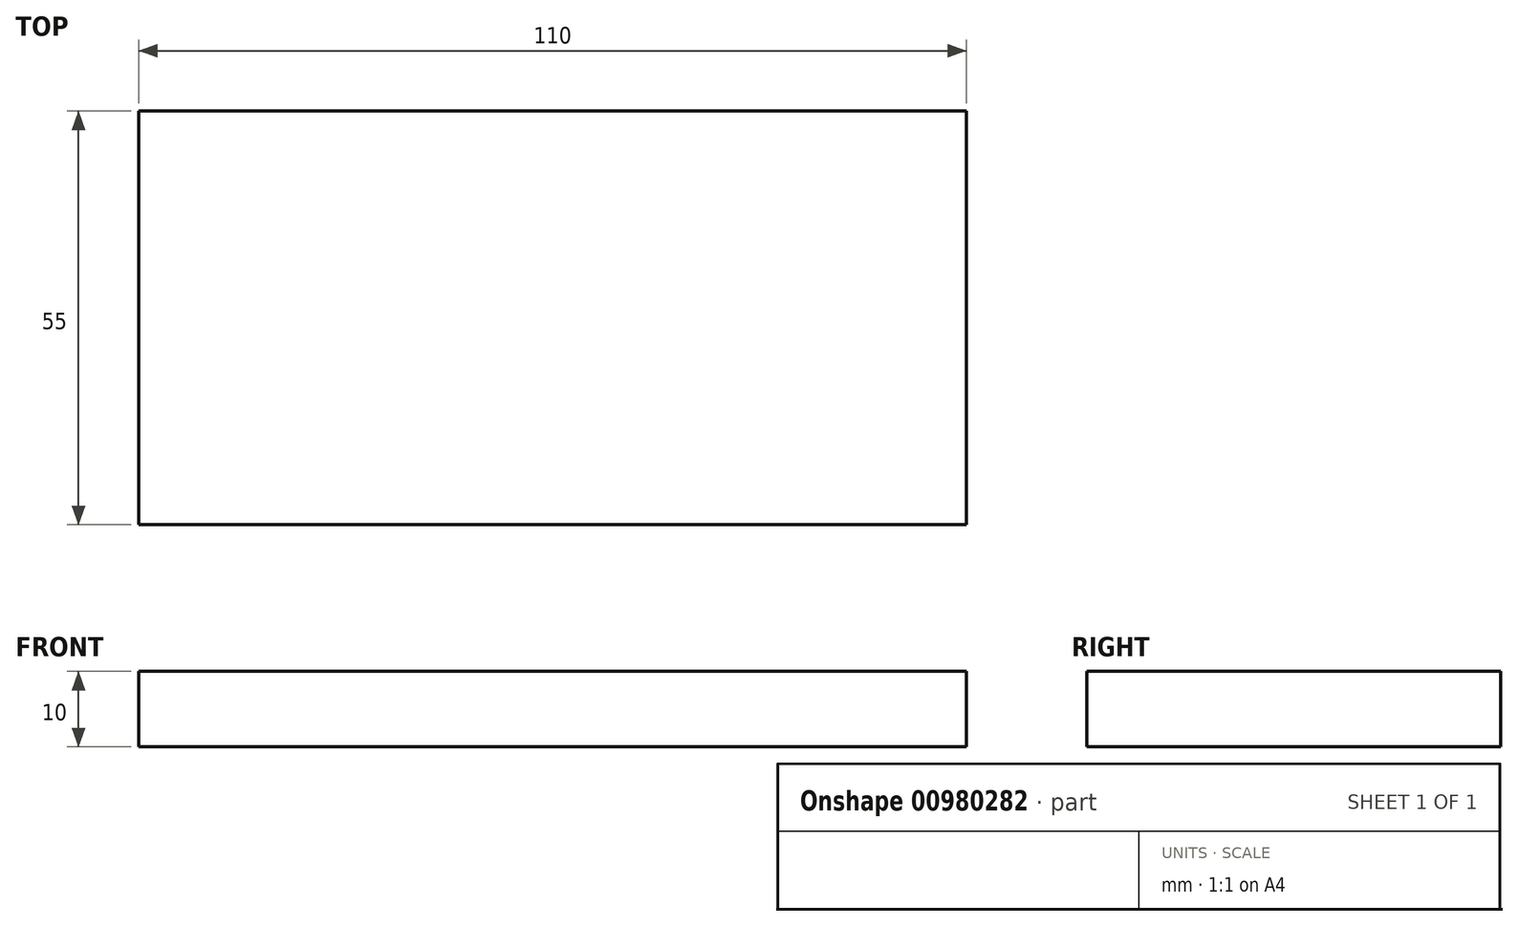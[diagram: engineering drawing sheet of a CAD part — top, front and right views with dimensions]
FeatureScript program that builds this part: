
annotation { "Feature Type Name" : "Feature", "Feature Type Description" : "" }
export const myFeature = defineFeature(function(context is Context, id is Id, definition is map)
    precondition{}
    {
        {
            var Q0;
            Q0=qCreatedBy(makeId("Top.planeOp"),FACE);
            var sketch = newSketch(context, id + "F0", { "sketchPlane" : qUnion([Q0])});
            skLineSegment(sketch, "E0.bottom", {"start": v(55, 27.5) * mm, "end": v(-55, 27.5) * mm});
            skLineSegment(sketch, "E0.top", {"start": v(55, -27.5) * mm, "end": v(-55, -27.5) * mm});
            skLineSegment(sketch, "E0.left", {"start": v(55, 27.5) * mm, "end": v(55, -27.5) * mm});
            skLineSegment(sketch, "E0.right", {"start": v(-55, 27.5) * mm, "end": v(-55, -27.5) * mm});
            skPoint(sketch, "E0.middle", {"position": v(0, 0) * mm});
            skSolve(sketch);
        }
        {
            var Q0;
            Q0 = qSketchRegion(id + "F0", true);
            extrude(context, id + "F1", {"entities" : qUnion([Q0]), "depth" : 10 * mm, "offsetDistance" : 25 * mm});
        }
    });
